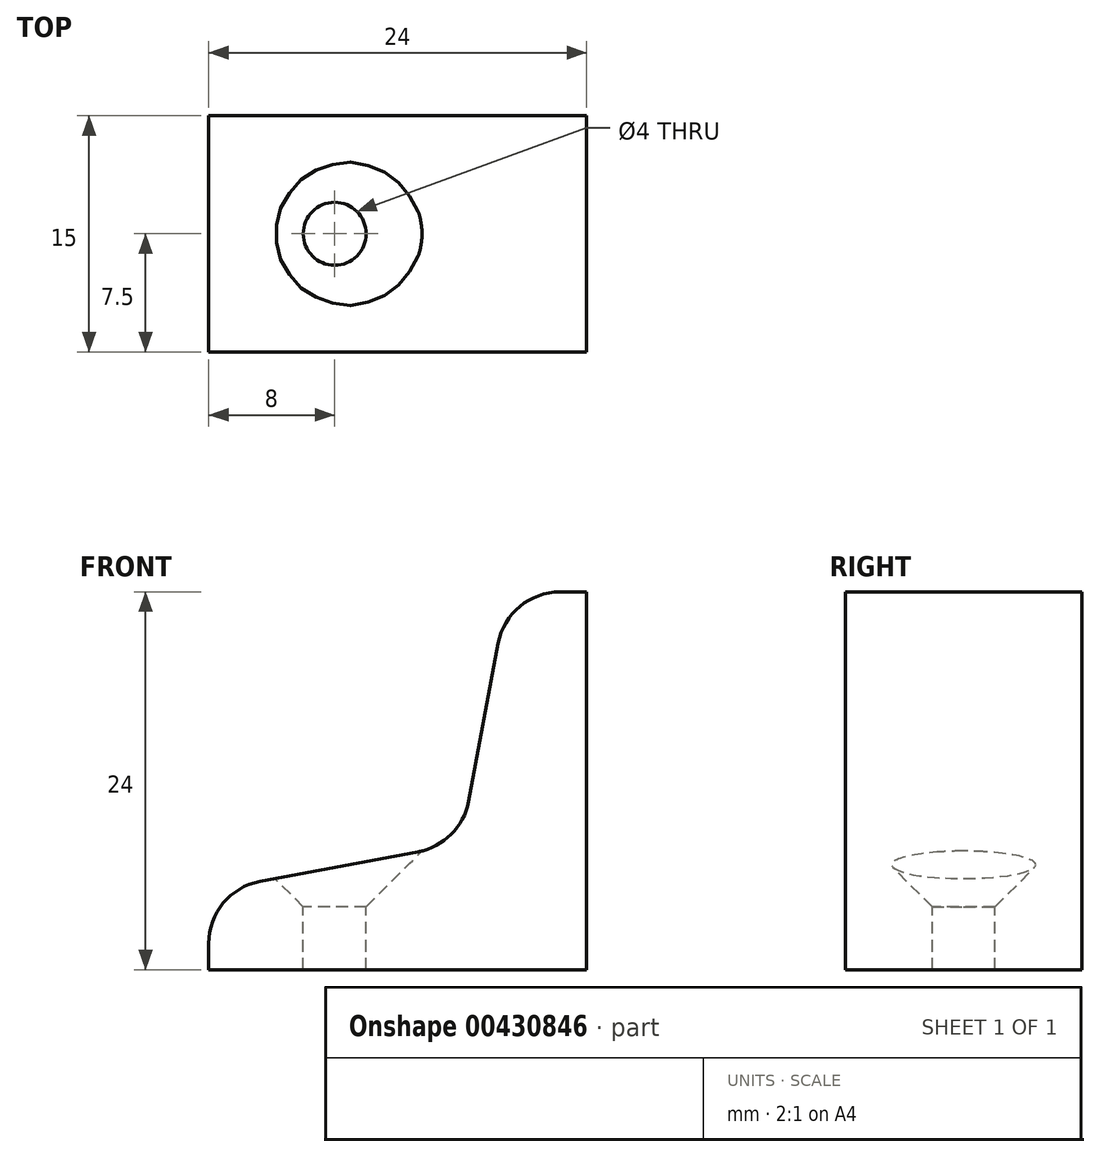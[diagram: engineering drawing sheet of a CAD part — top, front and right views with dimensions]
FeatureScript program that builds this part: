
annotation { "Feature Type Name" : "Feature", "Feature Type Description" : "" }
export const myFeature = defineFeature(function(context is Context, id is Id, definition is map)
    precondition{}
    {
        {
            var Q0;
            Q0=qCreatedBy(makeId("Front.planeOp"),FACE);
            var sketch = newSketch(context, id + "F0", { "sketchPlane" : qUnion([Q0])});
            skLineSegment(sketch, "E0", {"start": v(-24, 0) * mm, "end": v(0, 0) * mm});
            skLineSegment(sketch, "E1", {"start": v(0, 0) * mm, "end": v(0, 24) * mm});
            skLineSegment(sketch, "E2", {"start": v(0, 24) * mm, "end": v(-1.68, 24) * mm});
            skLineSegment(sketch, "E3", {"start": v(-5.61, 20.74) * mm, "end": v(-7.5, 10.69) * mm});
            skLineSegment(sketch, "E4", {"start": v(-10.69, 7.5) * mm, "end": v(-20.74, 5.61) * mm});
            skLineSegment(sketch, "E5", {"start": v(-24, 1.68) * mm, "end": v(-24, 0) * mm});
            skLineSegment(sketch, "E6", {"start": v(0, 0) * mm, "end": v(-24, 24) * mm, "construction": true});
            skPoint(sketch, "E7.visualSharp", {"position": v(-24, 5) * mm});
            skArc(sketch, "E7.filletArc", {"start": v(-20.74, 5.61) * mm, "mid": v(-23.08, 4.23) * mm, "end": v(-24, 1.68) * mm});
            skPoint(sketch, "E8.visualSharp", {"position": v(-8, 8) * mm});
            skArc(sketch, "E8.filletArc", {"start": v(-10.69, 7.5) * mm, "mid": v(-8.6, 8.6) * mm, "end": v(-7.5, 10.69) * mm});
            skPoint(sketch, "E9.visualSharp", {"position": v(-5, 24) * mm});
            skArc(sketch, "E9.filletArc", {"start": v(-1.68, 24) * mm, "mid": v(-4.23, 23.08) * mm, "end": v(-5.61, 20.74) * mm});
            skSolve(sketch);
        }
        {
            var Q0;
            Q0=makeQuery(id+"F0.imprint","IMPRINT",FACE,{"disambiguationData":[TD([[makeQuery(id+"F0.imprint","IMPRINT",EDGE,{"derivedFrom":sQuery(id+"F0.wireOp",EDGE,"E0")}),1.0]])]});
            extrude(context, id + "F1", {"entities" : qUnion([Q0]), "endBound" : BoundingType.SYMMETRIC, "depth" : 15 * mm});
        }
        {
            var Q0;
            Q0=qCreatedBy(makeId("Front.planeOp"),FACE);
            var sketch = newSketch(context, id + "F2", { "sketchPlane" : qUnion([Q0])});
            skLineSegment(sketch, "E10", {"start": v(-18, 0) * mm, "end": v(-18, 4) * mm});
            skLineSegment(sketch, "E11", {"start": v(-18, 4) * mm, "end": v(-22, 8) * mm});
            skLineSegment(sketch, "E12", {"start": v(-22, 8) * mm, "end": v(-16, 8) * mm});
            skLineSegment(sketch, "E13", {"start": v(-16, 0) * mm, "end": v(-18, 0) * mm});
            skLineSegment(sketch, "E14", {"start": v(-16, 0) * mm, "end": v(-16, 8) * mm});
            skLineSegment(sketch, "E15", {"start": v(-18, 4) * mm, "end": v(-14, 4) * mm, "construction": true});
            skPoint(sketch, "E16.start.orphan", {"position": v(-10, 8) * mm});
            skPoint(sketch, "E17.orphan", {"position": v(-14, 0) * mm});
            skLineSegment(sketch, "E18", {"start": v(-18, 0) * mm, "end": v(-16, 0) * mm});
            skSolve(sketch);
        }
        {
            var Q0;
            Q0=makeQuery(id+"F2.imprint","IMPRINT",FACE,{"disambiguationData":[TD([[makeQuery(id+"F2.imprint","IMPRINT",EDGE,{"derivedFrom":sQuery(id+"F2.wireOp",EDGE,"E10")}),-1.0]])]});
            var Q1;
            Q1=sQuery(id+"F2.wireOp",EDGE,"E14");
            revolve(context, id + "F3", {"operationType" : NewBodyOperationType.REMOVE, "entities" : qUnion([Q0]), "axis" : qUnion([Q1]), "revolveType" : RevolveType.FULL, "oppositeDirection" : true});
        }
    });
